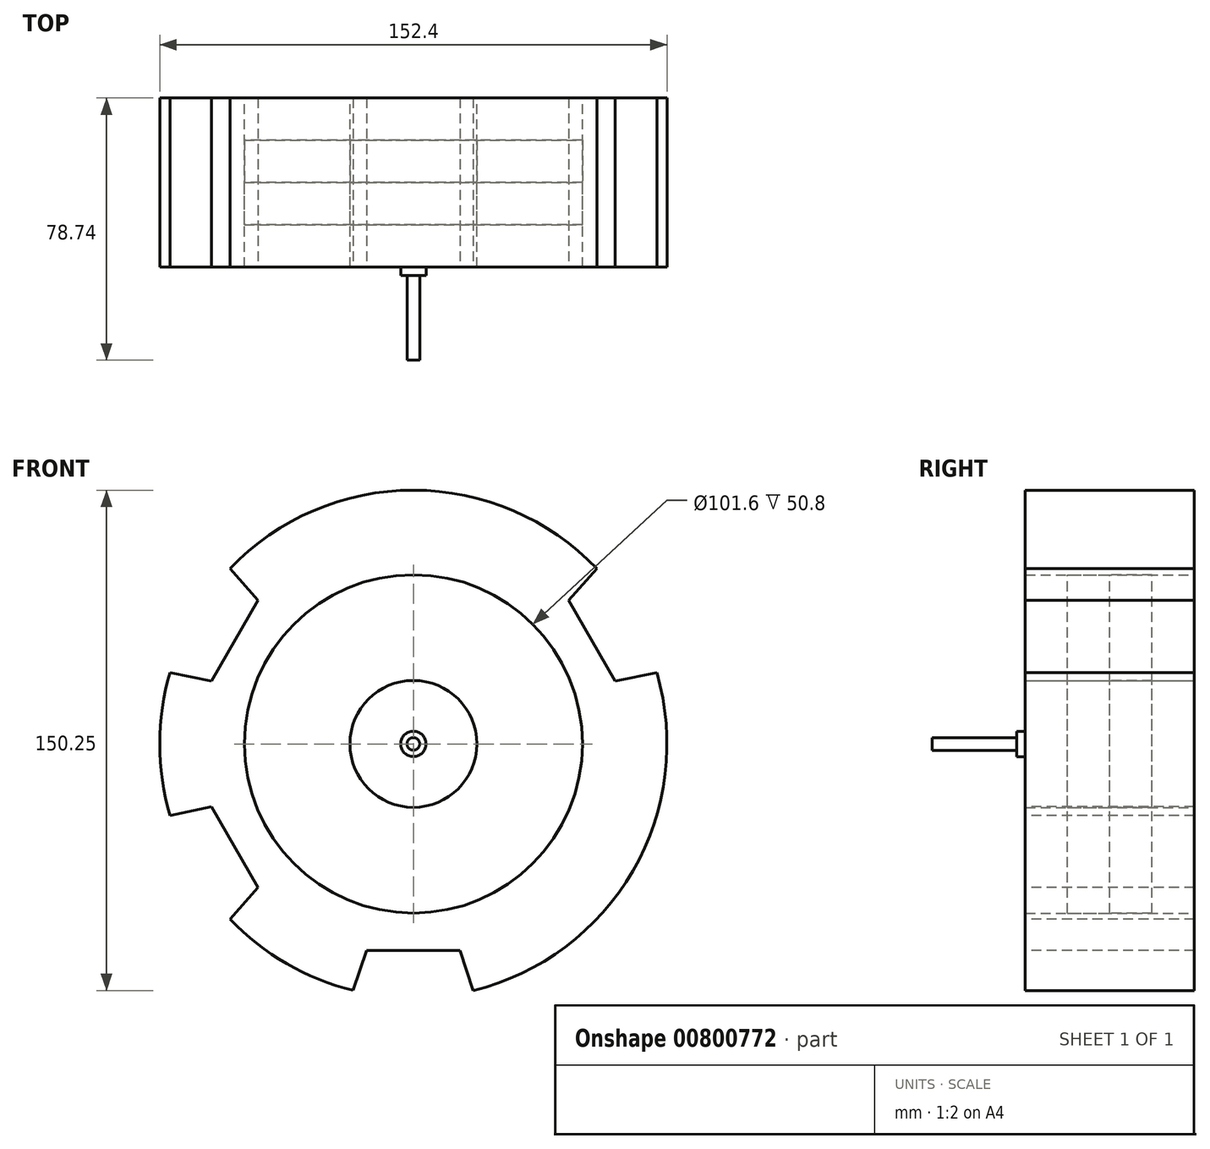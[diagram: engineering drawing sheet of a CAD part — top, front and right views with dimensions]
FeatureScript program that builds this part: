
annotation { "Feature Type Name" : "Feature", "Feature Type Description" : "" }
export const myFeature = defineFeature(function(context is Context, id is Id, definition is map)
    precondition{}
    {
        {
            var Q0;
            Q0=qCreatedBy(makeId("Front.planeOp"),FACE);
            var sketch = newSketch(context, id + "F0", { "sketchPlane" : qUnion([Q0])});
            skCircle(sketch, "E0", {"center": v(0, 0) * mm, "radius": 19.05 * mm});
            skCircle(sketch, "E1", {"center": v(0, 0) * mm, "radius": 50.8 * mm});
            skCircle(sketch, "E2", {"center": v(0, 0) * mm, "radius": 76.2 * mm});
            skSolve(sketch);
        }
        {
            var Q0;
            Q0 = qSketchRegion(id + "F0", true);
            extrude(context, id + "F1", {"entities" : qUnion([Q0]), "depth" : 25.4 * mm, "offsetDistance" : 25.4 * mm});
        }
        {
            var Q0;
            Q0=makeQuery(id+"F0.imprint","IMPRINT",FACE,{"disambiguationData":[TD([[makeQuery(id+"F0.imprint","IMPRINT",EDGE,{"derivedFrom":sQuery(id+"F0.wireOp",EDGE,"E0")}),1.0]])]});
            extrude(context, id + "F2", {"entities" : qUnion([Q0]), "depth" : 25.4 * mm, "offsetDistance" : 25.4 * mm});
        }
        {
            var Q0;
            Q0=makeQuery(id+"F0.imprint","IMPRINT",FACE,{"disambiguationData":[TD([[makeQuery(id+"F0.imprint","IMPRINT",EDGE,{"derivedFrom":sQuery(id+"F0.wireOp",EDGE,"E0")}),1.0]])]});
            extrude(context, id + "F3", {"entities" : qUnion([Q0]), "operationType" : NewBodyOperationType.ADD, "oppositeDirection" : true, "depth" : 25.4 * mm, "offsetDistance" : 25.4 * mm});
        }
        {
            var Q0;
            Q0=makeQuery(id+"F0.imprint","IMPRINT",FACE,{"disambiguationData":[TD([[makeQuery(id+"F0.imprint","IMPRINT",EDGE,{"derivedFrom":sQuery(id+"F0.wireOp",EDGE,"E1")}),-1.0]])]});
            extrude(context, id + "F4", {"entities" : qUnion([Q0]), "operationType" : NewBodyOperationType.ADD, "oppositeDirection" : true, "depth" : 25.4 * mm, "offsetDistance" : 25.4 * mm});
        }
        {
            var Q0;
            Q0=makeQuery(id+"F0.imprint","IMPRINT",FACE,{"disambiguationData":[TD([[makeQuery(id+"F0.imprint","IMPRINT",EDGE,{"derivedFrom":sQuery(id+"F0.wireOp",EDGE,"E0")}),-1.0]])]});
            extrude(context, id + "F5", {"entities" : qUnion([Q0]), "depth" : 12.7 * mm, "offsetDistance" : 25.4 * mm});
        }
        {
            var Q0;
            Q0=makeQuery(id+"F0.imprint","IMPRINT",FACE,{"disambiguationData":[TD([[makeQuery(id+"F0.imprint","IMPRINT",EDGE,{"derivedFrom":sQuery(id+"F0.wireOp",EDGE,"E0")}),-1.0]])]});
            extrude(context, id + "F6", {"entities" : qUnion([Q0]), "oppositeDirection" : true, "depth" : 12.7 * mm, "offsetDistance" : 25.4 * mm});
        }
        {
            var Q0;
            Q0=makeQuery(id+"F1.opExtrude","CAP_FACE",FACE,{"disambiguationData":[OSD([sQuery(id+"F0.wireOp",EDGE,"E1"),sQuery(id+"F0.wireOp",EDGE,"E2")])],"isStart":false});
            var sketch = newSketch(context, id + "F7", { "sketchPlane" : qUnion([Q0])});
            skLineSegment(sketch, "E3", {"start": v(-18.05, 74.03) * mm, "end": v(-13.98, 62) * mm});
            skLineSegment(sketch, "E4", {"start": v(-13.98, 62) * mm, "end": v(13.96, 62) * mm});
            skLineSegment(sketch, "E5", {"start": v(13.96, 62) * mm, "end": v(17.97, 74.05) * mm});
            skLineSegment(sketch, "E6.1.0", {"start": v(-55.09, -52.65) * mm, "end": v(-46.7, -43.1) * mm});
            skLineSegment(sketch, "E6.1.1", {"start": v(-46.7, -43.1) * mm, "end": v(-60.67, -18.91) * mm});
            skLineSegment(sketch, "E6.1.2", {"start": v(-60.67, -18.91) * mm, "end": v(-73.12, -21.46) * mm});
            skLineSegment(sketch, "E6.2.0", {"start": v(73.14, -21.38) * mm, "end": v(60.68, -18.9) * mm});
            skLineSegment(sketch, "E6.2.1", {"start": v(60.68, -18.9) * mm, "end": v(46.71, -43.09) * mm});
            skLineSegment(sketch, "E6.2.2", {"start": v(46.71, -43.09) * mm, "end": v(55.14, -52.6) * mm});
            skPoint(sketch, "E6.center", {"position": v(0, 0) * mm});
            skSolve(sketch);
        }
        {
            var Q0;
            {var subQ0=sQuery(id+"F7.wireOp",EDGE,"E5");Q0=makeQuery(id+"F7.imprint","IMPRINT",FACE,{"disambiguationData":[TD([[makeQuery(id+"F7.imprint","IMPRINT",EDGE,{"derivedFrom":subQ0}),1.0]])]});}
            var Q1;
            {var subQ0=sQuery(id+"F7.wireOp",EDGE,"E6.1.0");Q1=makeQuery(id+"F7.imprint","IMPRINT",FACE,{"disambiguationData":[TD([[makeQuery(id+"F7.imprint","IMPRINT",EDGE,{"derivedFrom":subQ0}),1.0]])]});}
            var Q2;
            {var subQ0=sQuery(id+"F7.wireOp",EDGE,"E6.2.2");Q2=makeQuery(id+"F7.imprint","IMPRINT",FACE,{"disambiguationData":[TD([[makeQuery(id+"F7.imprint","IMPRINT",EDGE,{"derivedFrom":subQ0}),1.0]])]});}
            extrude(context, id + "F8", {"entities" : qUnion([Q0, Q1, Q2]), "operationType" : NewBodyOperationType.REMOVE, "endBound" : BoundingType.THROUGH_ALL, "oppositeDirection" : true, "depth" : 25.4 * mm, "offsetDistance" : 25.4 * mm});
        }
        {
            var Q0;
            Q0=makeQuery(id+"F1.opExtrude","CAP_FACE",FACE,{"disambiguationData":[OSD([sQuery(id+"F0.wireOp",EDGE,"E1"),sQuery(id+"F0.wireOp",EDGE,"E2")])],"isStart":false});
            var sketch = newSketch(context, id + "F9", { "sketchPlane" : qUnion([Q0])});
            skLineSegment(sketch, "E7", {"start": v(-18.05, -74.03) * mm, "end": v(-13.98, -62) * mm});
            skLineSegment(sketch, "E8", {"start": v(-13.98, -62) * mm, "end": v(13.96, -62) * mm});
            skLineSegment(sketch, "E9", {"start": v(13.96, -62) * mm, "end": v(17.97, -74.05) * mm});
            skLineSegment(sketch, "E10.1.0", {"start": v(73.14, 21.38) * mm, "end": v(60.68, 18.9) * mm});
            skLineSegment(sketch, "E10.1.1", {"start": v(60.68, 18.9) * mm, "end": v(46.71, 43.09) * mm});
            skLineSegment(sketch, "E10.1.2", {"start": v(46.71, 43.09) * mm, "end": v(55.14, 52.6) * mm});
            skLineSegment(sketch, "E10.2.0", {"start": v(-55.09, 52.65) * mm, "end": v(-46.7, 43.1) * mm});
            skLineSegment(sketch, "E10.2.1", {"start": v(-46.7, 43.1) * mm, "end": v(-60.67, 18.91) * mm});
            skLineSegment(sketch, "E10.2.2", {"start": v(-60.67, 18.91) * mm, "end": v(-73.12, 21.46) * mm});
            skPoint(sketch, "E10.center", {"position": v(0, 0) * mm});
            skSolve(sketch);
        }
        {
            var Q0;
            {var subQ0=sQuery(id+"F9.wireOp",EDGE,"E10.2.0");Q0=makeQuery(id+"F9.imprint","IMPRINT",FACE,{"disambiguationData":[TD([[makeQuery(id+"F9.imprint","IMPRINT",EDGE,{"derivedFrom":subQ0}),-1.0]])]});}
            var Q1;
            {var subQ0=sQuery(id+"F9.wireOp",EDGE,"E10.1.0");Q1=makeQuery(id+"F9.imprint","IMPRINT",FACE,{"disambiguationData":[TD([[makeQuery(id+"F9.imprint","IMPRINT",EDGE,{"derivedFrom":subQ0}),-1.0]])]});}
            var Q2;
            {var subQ0=sQuery(id+"F9.wireOp",EDGE,"E7");Q2=makeQuery(id+"F9.imprint","IMPRINT",FACE,{"disambiguationData":[TD([[makeQuery(id+"F9.imprint","IMPRINT",EDGE,{"derivedFrom":subQ0}),-1.0]])]});}
            extrude(context, id + "F10", {"entities" : qUnion([Q0, Q1, Q2]), "operationType" : NewBodyOperationType.REMOVE, "endBound" : BoundingType.THROUGH_ALL, "oppositeDirection" : true, "depth" : 25.4 * mm, "offsetDistance" : 25.4 * mm});
        }
        {
            var Q0;
            Q0=makeQuery(id+"F2.opExtrude","CAP_FACE",FACE,{"disambiguationData":[OSD([sQuery(id+"F0.wireOp",EDGE,"E0")])],"isStart":false});
            var sketch = newSketch(context, id + "F11", { "sketchPlane" : qUnion([Q0])});
            skCircle(sketch, "E11", {"center": v(0, 0) * mm, "radius": 3.81 * mm});
            skSolve(sketch);
        }
        {
            var Q0;
            Q0 = qSketchRegion(id + "F11", true);
            extrude(context, id + "F12", {"entities" : qUnion([Q0]), "operationType" : NewBodyOperationType.ADD, "depth" : 2.54 * mm, "offsetDistance" : 25.4 * mm});
        }
        {
            var Q0;
            Q0=makeQuery(id+"F12.opExtrude","CAP_FACE",FACE,{"disambiguationData":[OSD([sQuery(id+"F11.wireOp",EDGE,"E11")])],"isStart":false});
            var sketch = newSketch(context, id + "F13", { "sketchPlane" : qUnion([Q0])});
            skCircle(sketch, "E12", {"center": v(0, 0) * mm, "radius": 1.9 * mm});
            skSolve(sketch);
        }
        {
            var Q0;
            Q0 = qSketchRegion(id + "F13", true);
            extrude(context, id + "F14", {"entities" : qUnion([Q0]), "operationType" : NewBodyOperationType.ADD, "depth" : 25.4 * mm, "offsetDistance" : 25.4 * mm});
        }
    });
